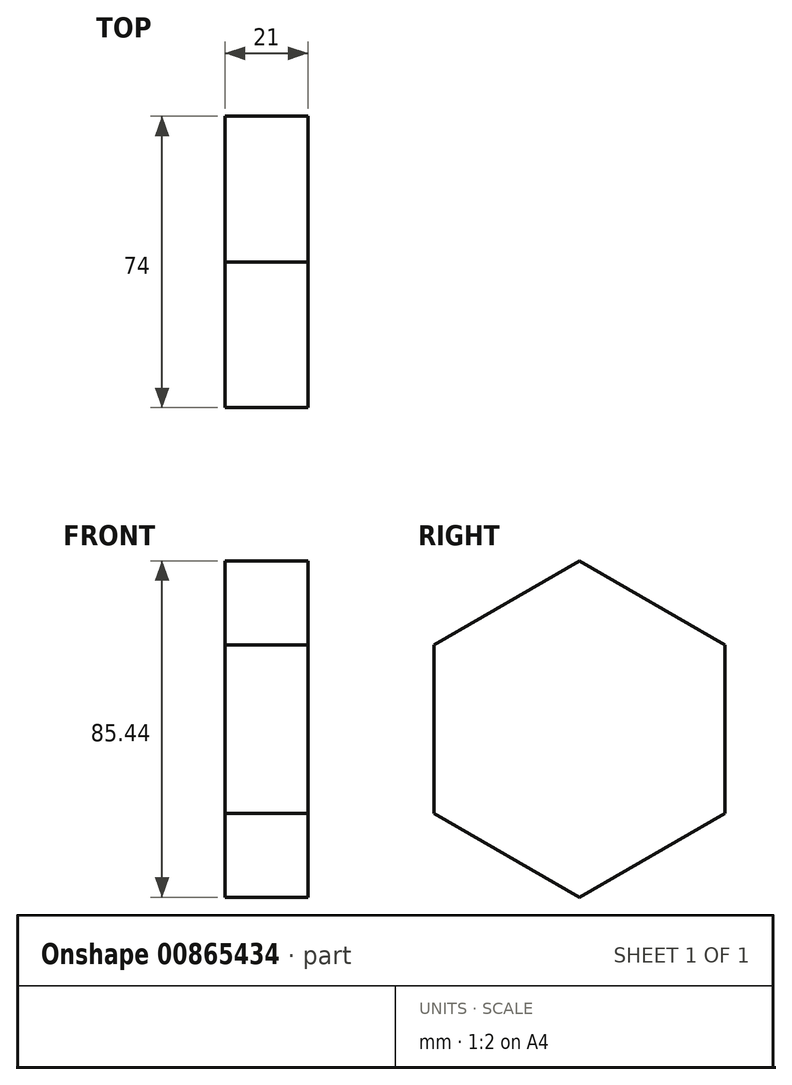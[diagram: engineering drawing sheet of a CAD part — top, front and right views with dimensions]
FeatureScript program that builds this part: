
annotation { "Feature Type Name" : "Feature", "Feature Type Description" : "" }
export const myFeature = defineFeature(function(context is Context, id is Id, definition is map)
    precondition{}
    {
        {
            var Q0;
            Q0=qCreatedBy(makeId("Right.planeOp"),FACE);
            cPlane(context, id + "F0", {"entities" : qUnion([Q0]), "cplaneType" : CPlaneType.OFFSET, "offset" : (140 / 2) * mm, "oppositeDirection" : true, "width" : 150 * mm, "height" : 150 * mm});
        }
        {
            var Q0;
            Q0=qCreatedBy(id+"F0.planeOp",FACE);
            var sketch = newSketch(context, id + "F1", { "sketchPlane" : qUnion([Q0])});
            skCircle(sketch, "E0.cCircle", {"center": v(0, 0) * mm, "radius": 37 * mm, "construction": true});
            skLineSegment(sketch, "E0.0", {"start": v(37, -21.36) * mm, "end": v(0, -42.72) * mm});
            skLineSegment(sketch, "E0.1", {"start": v(0, -42.72) * mm, "end": v(-37, -21.36) * mm});
            skLineSegment(sketch, "E0.2", {"start": v(-37, -21.36) * mm, "end": v(-37, 21.36) * mm});
            skLineSegment(sketch, "E0.3", {"start": v(-37, 21.36) * mm, "end": v(0, 42.72) * mm});
            skLineSegment(sketch, "E0.4", {"start": v(0, 42.72) * mm, "end": v(37, 21.36) * mm});
            skLineSegment(sketch, "E0.5", {"start": v(37, 21.36) * mm, "end": v(37, -21.36) * mm});
            skPoint(sketch, "E0.0.midPoint", {"position": v(18.5, -32.04) * mm});
            skSolve(sketch);
        }
        {
            var Q0;
            Q0 = qSketchRegion(id + "F1", true);
            var Q1;
            Q1=sQuery(id+"F1.wireOp",EDGE,"E0.4");
            var Q2;
            Q2=sQuery(id+"F1.wireOp",EDGE,"E0.5");
            var Q3;
            Q3=sQuery(id+"F1.wireOp",EDGE,"E0.0");
            var Q4;
            Q4=sQuery(id+"F1.wireOp",EDGE,"E0.1");
            var Q5;
            Q5=sQuery(id+"F1.wireOp",EDGE,"E0.2");
            var Q6;
            Q6=sQuery(id+"F1.wireOp",EDGE,"E0.3");
            extrude(context, id + "F2", {"entities" : qUnion([Q0]), "bodyType" : ToolBodyType.SURFACE, "surfaceEntities" : qUnion([Q1, Q2, Q3, Q4, Q5, Q6]), "depth" : 21 * mm, "offsetDistance" : 25 * mm});
        }
    });
